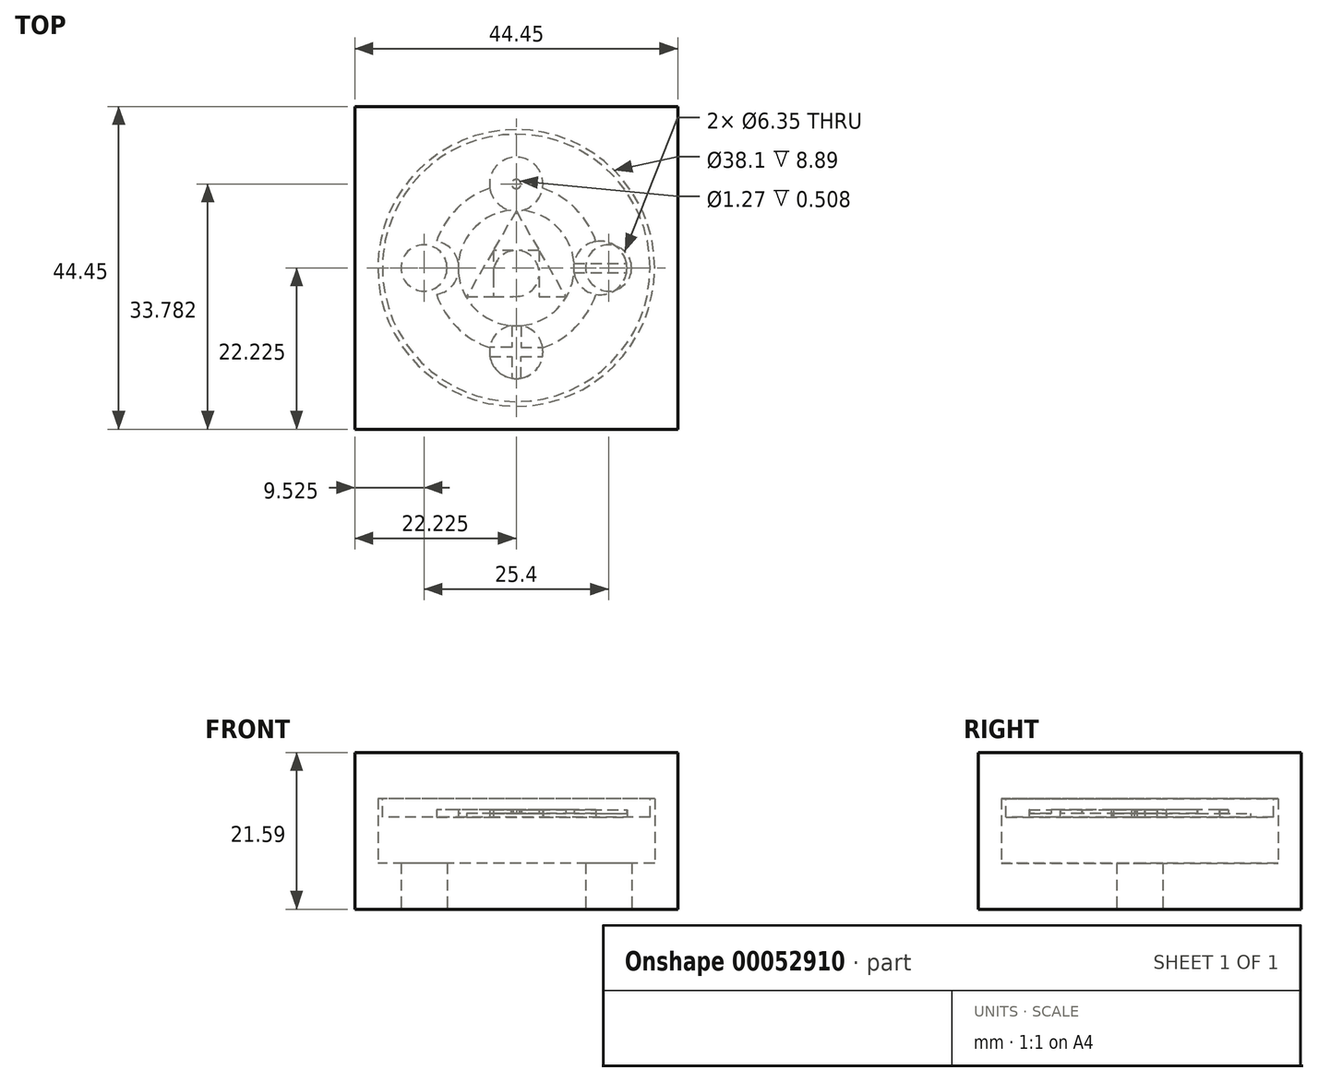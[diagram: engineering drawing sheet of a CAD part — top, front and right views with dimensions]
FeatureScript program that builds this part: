
annotation { "Feature Type Name" : "Feature", "Feature Type Description" : "" }
export const myFeature = defineFeature(function(context is Context, id is Id, definition is map)
    precondition{}
    {
        {
            var Q0;
            Q0=qCreatedBy(makeId("Top.planeOp"),FACE);
            var sketch = newSketch(context, id + "F0", { "sketchPlane" : qUnion([Q0])});
            skLineSegment(sketch, "E0.bottom", {"start": v(0, 0) * mm, "end": v(44.45, 0) * mm});
            skLineSegment(sketch, "E0.top", {"start": v(0, 44.45) * mm, "end": v(44.45, 44.45) * mm});
            skLineSegment(sketch, "E0.left", {"start": v(0, 0) * mm, "end": v(0, 44.45) * mm});
            skLineSegment(sketch, "E0.right", {"start": v(44.45, 0) * mm, "end": v(44.45, 44.45) * mm});
            skCircle(sketch, "E1", {"center": v(22.22, 22.23) * mm, "radius": 19.05 * mm});
            skPoint(sketch, "E1.centerSnap0", {"position": v(0, 22.23) * mm});
            skPoint(sketch, "E1.centerSnap1", {"position": v(22.23, 0) * mm});
            skCircle(sketch, "E2", {"center": v(9.52, 22.23) * mm, "radius": 3.18 * mm});
            skCircle(sketch, "E3", {"center": v(34.92, 22.23) * mm, "radius": 3.18 * mm});
            skSolve(sketch);
        }
        {
            var Q0;
            Q0=makeQuery(id+"F0.imprint","IMPRINT",FACE,{"disambiguationData":[TD([[makeQuery(id+"F0.imprint","IMPRINT",EDGE,{"derivedFrom":sQuery(id+"F0.wireOp",EDGE,"E0.bottom")}),1.0]])]});
            extrude(context, id + "F1", {"entities" : qUnion([Q0]), "depth" : 15.24 * mm});
        }
        {
            var Q0;
            Q0=makeQuery(id+"F0.imprint","IMPRINT",FACE,{"disambiguationData":[TD([[makeQuery(id+"F0.imprint","IMPRINT",EDGE,{"derivedFrom":sQuery(id+"F0.wireOp",EDGE,"E1")}),1.0]])]});
            extrude(context, id + "F2", {"entities" : qUnion([Q0]), "operationType" : NewBodyOperationType.ADD, "depth" : 6.35 * mm});
        }
        {
            var Q0;
            Q0=makeQuery(id+"F1.opExtrude","CAP_FACE",FACE,{"disambiguationData":[OSD([sQuery(id+"F0.wireOp",EDGE,"E0.bottom"),sQuery(id+"F0.wireOp",EDGE,"E0.top"),sQuery(id+"F0.wireOp",EDGE,"E0.left"),sQuery(id+"F0.wireOp",EDGE,"E0.right"),sQuery(id+"F0.wireOp",EDGE,"E1")])],"isStart":false});
            var sketch = newSketch(context, id + "F3", { "sketchPlane" : qUnion([Q0])});
            skCircle(sketch, "E4", {"center": v(22.22, 22.23) * mm, "radius": 18.41 * mm});
            skLineSegment(sketch, "E5.rect.bottom", {"start": v(0, 0) * mm, "end": v(44.45, 0) * mm});
            skLineSegment(sketch, "E5.rect.top", {"start": v(0, 44.45) * mm, "end": v(44.45, 44.45) * mm});
            skLineSegment(sketch, "E5.rect.left", {"start": v(0, 0) * mm, "end": v(0, 44.45) * mm});
            skLineSegment(sketch, "E5.rect.right", {"start": v(44.45, 0) * mm, "end": v(44.45, 44.45) * mm});
            skSolve(sketch);
        }
        {
            var Q0;
            Q0=makeQuery(id+"F3.imprint","IMPRINT",FACE,{"disambiguationData":[TD([[makeQuery(id+"F3.imprint","IMPRINT",EDGE,{"derivedFrom":sQuery(id+"F3.wireOp",EDGE,"E4")}),1.0]])]});
            extrude(context, id + "F4", {"entities" : qUnion([Q0]), "oppositeDirection" : true, "depth" : 2.54 * mm});
        }
        {
            var Q0;
            Q0=makeQuery(id+"F3.imprint","IMPRINT",FACE,{"disambiguationData":[TD([[makeQuery(id+"F3.imprint","IMPRINT",EDGE,{"derivedFrom":sQuery(id+"F3.wireOp",EDGE,"E4")}),1.0]])]});
            var Q1;
            Q1=makeQuery(id+"F3.imprint","IMPRINT",FACE,{"disambiguationData":[TD([[makeQuery(id+"F3.imprint","IMPRINT",EDGE,{"derivedFrom":sQuery(id+"F3.wireOp",EDGE,"E5.rect.bottom")}),1.0]])]});
            var Q2;
            Q2=makeQuery(id+"F3.imprint","IMPRINT",FACE,{"disambiguationData":[TD([[makeQuery(id+"F3.imprint","IMPRINT",EDGE,{"derivedFrom":sQuery(id+"F3.wireOp",EDGE,"E4")}),-1.0]])]});
            extrude(context, id + "F5", {"entities" : qUnion([Q0, Q1, Q2]), "operationType" : NewBodyOperationType.ADD, "depth" : 6.35 * mm});
        }
        {
            var Q0;
            Q0=makeQuery(id+"F4.opExtrude","CAP_FACE",FACE,{"disambiguationData":[OSD([sQuery(id+"F3.wireOp",EDGE,"E4")])],"isStart":false});
            var sketch = newSketch(context, id + "F6", { "sketchPlane" : qUnion([Q0])});
            skCircle(sketch, "E6.0.0", {"center": v(22.22, -22.23) * mm, "radius": 18.41 * mm});
            skArc(sketch, "E7", {"start": v(30.18, -22.86) * mm, "mid": v(30.2, -22.23) * mm, "end": v(30.18, -21.6) * mm});
            skLineSegment(sketch, "E8", {"start": v(15.42, -18.3) * mm, "end": v(21.82, -18.3) * mm});
            skPoint(sketch, "E9.endSnap0", {"position": v(22.22, -18.3) * mm});
            skLineSegment(sketch, "E10", {"start": v(22.23, -30.08) * mm, "end": v(15.42, -18.3) * mm});
            skLineSegment(sketch, "E11.bottom", {"start": v(25.4, -24.64) * mm, "end": v(22.63, -24.64) * mm});
            skLineSegment(sketch, "E11.top", {"start": v(25.4, -18.3) * mm, "end": v(22.63, -18.3) * mm});
            skLineSegment(sketch, "E11.left", {"start": v(25.4, -24.64) * mm, "end": v(25.4, -21.87) * mm});
            skLineSegment(sketch, "E11.right", {"start": v(19.06, -24.64) * mm, "end": v(19.06, -21.87) * mm});
            skCircle(sketch, "E12", {"center": v(22.22, -21.47) * mm, "radius": 3.17 * mm});
            skPoint(sketch, "E12.first.point", {"position": v(25.4, -21.47) * mm});
            skPoint(sketch, "E12.second.point", {"position": v(19.06, -21.47) * mm});
            skPoint(sketch, "E12.third.point", {"position": v(22.22, -24.64) * mm});
            skLineSegment(sketch, "E13", {"start": v(22.22, -30.08) * mm, "end": v(29.03, -18.3) * mm});
            skArc(sketch, "E14", {"start": v(14.28, -21.5) * mm, "mid": v(6.98, -22.23) * mm, "end": v(14.28, -22.95) * mm});
            skArc(sketch, "E15", {"start": v(22.86, -14.3) * mm, "mid": v(22.22, -6.99) * mm, "end": v(21.59, -14.3) * mm});
            skArc(sketch, "E16", {"start": v(30.15, -22.86) * mm, "mid": v(37.46, -22.23) * mm, "end": v(30.15, -21.6) * mm});
            skArc(sketch, "E17", {"start": v(11.25, -25.86) * mm, "mid": v(14.05, -30.4) * mm, "end": v(18.59, -33.2) * mm});
            skArc(sketch, "E18.trimOffspring", {"start": v(18.59, -11.25) * mm, "mid": v(14.05, -14.05) * mm, "end": v(11.25, -18.59) * mm});
            skArc(sketch, "E19.trimOffspring", {"start": v(33.2, -18.59) * mm, "mid": v(30.4, -14.05) * mm, "end": v(25.86, -11.25) * mm});
            skArc(sketch, "E20.trimOffspring", {"start": v(25.86, -33.2) * mm, "mid": v(30.4, -30.4) * mm, "end": v(33.2, -25.86) * mm});
            skCircle(sketch, "E21", {"center": v(22.22, -33.78) * mm, "radius": 0.64 * mm});
            skLineSegment(sketch, "E22", {"start": v(30.15, -22.86) * mm, "end": v(37.4, -22.86) * mm});
            skLineSegment(sketch, "E23", {"start": v(30.15, -21.6) * mm, "end": v(37.4, -21.6) * mm});
            skLineSegment(sketch, "E24", {"start": v(21.59, -14.3) * mm, "end": v(21.59, -11.3) * mm});
            skLineSegment(sketch, "E25", {"start": v(21.59, -11.3) * mm, "end": v(18.6, -11.3) * mm});
            skLineSegment(sketch, "E26", {"start": v(18.6, -10.03) * mm, "end": v(21.59, -10.03) * mm});
            skLineSegment(sketch, "E27", {"start": v(21.59, -10.03) * mm, "end": v(21.59, -7.04) * mm});
            skLineSegment(sketch, "E28", {"start": v(22.86, -7.04) * mm, "end": v(22.86, -10.03) * mm});
            skLineSegment(sketch, "E29", {"start": v(22.86, -10.03) * mm, "end": v(25.85, -10.03) * mm});
            skLineSegment(sketch, "E30", {"start": v(22.86, -14.3) * mm, "end": v(22.86, -11.3) * mm});
            skLineSegment(sketch, "E31", {"start": v(22.86, -11.3) * mm, "end": v(25.85, -11.3) * mm});
            skArc(sketch, "E32.trimOffspring", {"start": v(21.5, -30.17) * mm, "mid": v(22.22, -37.46) * mm, "end": v(22.95, -30.17) * mm});
            skArc(sketch, "E33.trimOffspring", {"start": v(30.17, -21.5) * mm, "mid": v(27.87, -16.58) * mm, "end": v(22.95, -14.28) * mm});
            skArc(sketch, "E34.trimOffspring", {"start": v(22.86, -14.27) * mm, "mid": v(22.23, -14.25) * mm, "end": v(21.59, -14.27) * mm});
            skArc(sketch, "E35.trimOffspring", {"start": v(21.5, -14.28) * mm, "mid": v(16.58, -27.87) * mm, "end": v(30.17, -22.95) * mm});
            skLineSegment(sketch, "E36", {"start": v(19.06, -21.87) * mm, "end": v(19.08, -21.87) * mm});
            skLineSegment(sketch, "E37", {"start": v(19.06, -21.07) * mm, "end": v(19.08, -21.07) * mm});
            skLineSegment(sketch, "E38", {"start": v(21.82, -18.32) * mm, "end": v(21.82, -18.3) * mm});
            skLineSegment(sketch, "E39", {"start": v(22.63, -18.32) * mm, "end": v(22.63, -18.3) * mm});
            skLineSegment(sketch, "E40", {"start": v(25.37, -21.07) * mm, "end": v(25.4, -21.07) * mm});
            skLineSegment(sketch, "E41", {"start": v(25.37, -21.87) * mm, "end": v(25.4, -21.87) * mm});
            skLineSegment(sketch, "E42", {"start": v(22.63, -24.61) * mm, "end": v(22.63, -24.64) * mm});
            skLineSegment(sketch, "E43", {"start": v(21.82, -24.61) * mm, "end": v(21.82, -24.64) * mm});
            skLineSegment(sketch, "E44.trimOffspring", {"start": v(19.06, -21.07) * mm, "end": v(19.06, -18.3) * mm});
            skLineSegment(sketch, "E45.trimOffspring", {"start": v(21.82, -24.64) * mm, "end": v(19.06, -24.64) * mm});
            skLineSegment(sketch, "E46.trimOffspring", {"start": v(25.4, -21.07) * mm, "end": v(25.4, -18.3) * mm});
            skLineSegment(sketch, "E47.trimOffspring", {"start": v(21.82, -18.3) * mm, "end": v(19.06, -18.3) * mm});
            skLineSegment(sketch, "E48.trimOffspring", {"start": v(22.63, -18.3) * mm, "end": v(29.03, -18.3) * mm});
            skSolve(sketch);
        }
        {
            var Q0;
            {var subQ0=sQuery(id+"F6.wireOp",EDGE,"E26");Q0=makeQuery(id+"F6.imprint","IMPRINT",FACE,{"disambiguationData":[TD([[makeQuery(id+"F6.imprint","IMPRINT",EDGE,{"derivedFrom":subQ0}),1.0]])]});}
            var Q1;
            {var subQ0=sQuery(id+"F6.wireOp",EDGE,"E28");Q1=makeQuery(id+"F6.imprint","IMPRINT",FACE,{"disambiguationData":[TD([[makeQuery(id+"F6.imprint","IMPRINT",EDGE,{"derivedFrom":subQ0}),1.0]])]});}
            var Q2;
            Q2=makeQuery(id+"F6.imprint","IMPRINT",FACE,{"disambiguationData":[TD([[makeQuery(id+"F6.imprint","IMPRINT",EDGE,{"derivedFrom":sQuery(id+"F6.wireOp",EDGE,"E21")}),-1.0]])]});
            var Q3;
            {var subQ4=sQuery(id+"F6.wireOp",EDGE,"E31");Q3=makeQuery(id+"F6.imprint","IMPRINT",FACE,{"disambiguationData":[TD([[makeQuery(id+"F6.imprint","IMPRINT",EDGE,{"derivedFrom":subQ4}),-1.0]])]});}
            var Q4;
            {var subQ0=sQuery(id+"F6.wireOp",EDGE,"E25");Q4=makeQuery(id+"F6.imprint","IMPRINT",FACE,{"disambiguationData":[TD([[makeQuery(id+"F6.imprint","IMPRINT",EDGE,{"derivedFrom":subQ0}),1.0]])]});}
            var Q5;
            {var subQ1=sQuery(id+"F6.wireOp",EDGE,"E16");var subQ4=makeQuery(id+"F6.imprint","INTERSECT",VERTEX,{"derivedFrom":[subQ1,sQuery(id+"F6.wireOp",EDGE,"E19.trimOffspring")]});Q5=makeQuery(id+"F6.imprint","IMPRINT",FACE,{"disambiguationData":[TD([[makeQuery(id+"F6.imprint","IMPRINT",EDGE,{"disambiguationData":[TD([[subQ4,1.0]])],"derivedFrom":subQ1}),1.0]])]});}
            var Q6;
            {var subQ0=sQuery(id+"F6.wireOp",EDGE,"E22");var subQ2=sQuery(id+"F6.wireOp",EDGE,"E16");var subQ3=makeQuery(id+"F6.imprint","INTERSECT",VERTEX,{"disambiguationData":[OD(0.0)],"derivedFrom":[subQ2,subQ0]});Q6=makeQuery(id+"F6.imprint","IMPRINT",FACE,{"disambiguationData":[TD([[makeQuery(id+"F6.imprint","IMPRINT",EDGE,{"disambiguationData":[TD([[subQ3,-1.0]])],"derivedFrom":subQ2}),1.0]])]});}
            var Q7;
            {var subQ0=sQuery(id+"F6.wireOp",EDGE,"E35.trimOffspring");var subQ1=sQuery(id+"F6.wireOp",EDGE,"E14");var subQ2=makeQuery(id+"F6.imprint","INTERSECT",VERTEX,{"disambiguationData":[OD(0.0)],"derivedFrom":[subQ1,subQ0]});Q7=makeQuery(id+"F6.imprint","IMPRINT",FACE,{"disambiguationData":[TD([[makeQuery(id+"F6.imprint","IMPRINT",EDGE,{"disambiguationData":[TD([[subQ2,-1.0]])],"derivedFrom":subQ1}),1.0]])]});}
            var Q8;
            {var subQ5=sQuery(id+"F6.wireOp",EDGE,"E37");Q8=makeQuery(id+"F6.imprint","IMPRINT",FACE,{"disambiguationData":[TD([[makeQuery(id+"F6.imprint","IMPRINT",EDGE,{"derivedFrom":subQ5}),1.0]])]});}
            var Q9;
            {var subQ5=sQuery(id+"F6.wireOp",EDGE,"E36");Q9=makeQuery(id+"F6.imprint","IMPRINT",FACE,{"disambiguationData":[TD([[makeQuery(id+"F6.imprint","IMPRINT",EDGE,{"derivedFrom":subQ5}),-1.0]])]});}
            var Q10;
            {var subQ1=sQuery(id+"F6.wireOp",EDGE,"E11.bottom");var subQ3=sQuery(id+"F6.wireOp",EDGE,"E12");var subQ4=makeQuery(id+"F6.imprint","INTERSECT",VERTEX,{"derivedFrom":[subQ1,subQ3]});Q10=makeQuery(id+"F6.imprint","IMPRINT",FACE,{"disambiguationData":[TD([[makeQuery(id+"F6.imprint","IMPRINT",EDGE,{"disambiguationData":[TD([[subQ4,-1.0]])],"derivedFrom":subQ3}),-1.0]])]});}
            var Q11;
            {var subQ1=sQuery(id+"F6.wireOp",EDGE,"E11.top");var subQ3=sQuery(id+"F6.wireOp",EDGE,"E12");var subQ4=makeQuery(id+"F6.imprint","INTERSECT",VERTEX,{"derivedFrom":[subQ1,subQ3]});Q11=makeQuery(id+"F6.imprint","IMPRINT",FACE,{"disambiguationData":[TD([[makeQuery(id+"F6.imprint","IMPRINT",EDGE,{"disambiguationData":[TD([[subQ4,1.0]])],"derivedFrom":subQ3}),-1.0]])]});}
            var Q12;
            {var subQ5=sQuery(id+"F6.wireOp",EDGE,"E41");Q12=makeQuery(id+"F6.imprint","IMPRINT",FACE,{"disambiguationData":[TD([[makeQuery(id+"F6.imprint","IMPRINT",EDGE,{"derivedFrom":subQ5}),-1.0]])]});}
            var Q13;
            {var subQ10=sQuery(id+"F6.wireOp",EDGE,"E7");Q13=makeQuery(id+"F6.imprint","IMPRINT",FACE,{"disambiguationData":[TD([[makeQuery(id+"F6.imprint","IMPRINT",EDGE,{"derivedFrom":subQ10}),1.0]])]});}
            var Q14;
            {var subQ0=sQuery(id+"F6.wireOp",EDGE,"E11.left");var subQ1=sQuery(id+"F6.wireOp",EDGE,"E11.bottom");var subQ2=makeQuery(id+"F6.imprint","INTERSECT",VERTEX,{"derivedFrom":[subQ1,subQ0]});Q14=makeQuery(id+"F6.imprint","IMPRINT",FACE,{"disambiguationData":[TD([[makeQuery(id+"F6.imprint","IMPRINT",EDGE,{"disambiguationData":[TD([[subQ2,-1.0]])],"derivedFrom":subQ1}),-1.0]])]});}
            var Q15;
            {var subQ0=sQuery(id+"F6.wireOp",EDGE,"E45.trimOffspring");var subQ1=sQuery(id+"F6.wireOp",EDGE,"E10");var subQ2=makeQuery(id+"F6.imprint","INTERSECT",VERTEX,{"derivedFrom":[subQ1,subQ0]});Q15=makeQuery(id+"F6.imprint","IMPRINT",FACE,{"disambiguationData":[TD([[makeQuery(id+"F6.imprint","IMPRINT",EDGE,{"disambiguationData":[TD([[subQ2,-1.0]])],"derivedFrom":subQ1}),1.0]])]});}
            extrude(context, id + "F7", {"entities" : qUnion([Q0, Q1, Q2, Q3, Q4, Q5, Q6, Q7, Q8, Q9, Q10, Q11, Q12, Q13, Q14, Q15]), "operationType" : NewBodyOperationType.REMOVE, "oppositeDirection" : true, "depth" : 0.5 * mm});
        }
        {
            var Q0;
            {var subQ0=sQuery(id+"F6.wireOp",EDGE,"E18.trimOffspring");Q0=makeQuery(id+"F6.imprint","IMPRINT",FACE,{"disambiguationData":[TD([[makeQuery(id+"F6.imprint","IMPRINT",EDGE,{"derivedFrom":subQ0}),1.0]])]});}
            var Q1;
            {var subQ3=sQuery(id+"F6.wireOp",EDGE,"E17");Q1=makeQuery(id+"F6.imprint","IMPRINT",FACE,{"disambiguationData":[TD([[makeQuery(id+"F6.imprint","IMPRINT",EDGE,{"derivedFrom":subQ3}),1.0]])]});}
            var Q2;
            {var subQ0=sQuery(id+"F6.wireOp",EDGE,"E19.trimOffspring");Q2=makeQuery(id+"F6.imprint","IMPRINT",FACE,{"disambiguationData":[TD([[makeQuery(id+"F6.imprint","IMPRINT",EDGE,{"derivedFrom":subQ0}),1.0]])]});}
            var Q3;
            {var subQ5=sQuery(id+"F6.wireOp",EDGE,"E25");Q3=makeQuery(id+"F6.imprint","IMPRINT",FACE,{"disambiguationData":[TD([[makeQuery(id+"F6.imprint","IMPRINT",EDGE,{"derivedFrom":subQ5}),-1.0]])]});}
            var Q4;
            {var subQ0=sQuery(id+"F6.wireOp",EDGE,"E7");Q4=makeQuery(id+"F6.imprint","IMPRINT",FACE,{"disambiguationData":[TD([[makeQuery(id+"F6.imprint","IMPRINT",EDGE,{"derivedFrom":subQ0}),-1.0]])]});}
            var Q5;
            Q5=makeQuery(id+"F6.imprint","IMPRINT",FACE,{"disambiguationData":[TD([[makeQuery(id+"F6.imprint","IMPRINT",EDGE,{"derivedFrom":sQuery(id+"F6.wireOp",EDGE,"E21")}),1.0]])]});
            var Q6;
            {var subQ0=sQuery(id+"F6.wireOp",EDGE,"E12");var subQ6=makeQuery(id+"F6.imprint","INTERSECT",VERTEX,{"derivedFrom":[subQ0,sQuery(id+"F6.wireOp",EDGE,"E39")]});Q6=makeQuery(id+"F6.imprint","IMPRINT",FACE,{"disambiguationData":[TD([[makeQuery(id+"F6.imprint","IMPRINT",EDGE,{"disambiguationData":[TD([[subQ6,1.0]])],"derivedFrom":subQ0}),1.0]])]});}
            var Q7;
            {var subQ5=sQuery(id+"F6.wireOp",EDGE,"E42");Q7=makeQuery(id+"F6.imprint","IMPRINT",FACE,{"disambiguationData":[TD([[makeQuery(id+"F6.imprint","IMPRINT",EDGE,{"derivedFrom":subQ5}),-1.0]])]});}
            var Q8;
            {var subQ0=sQuery(id+"F6.wireOp",EDGE,"E40");Q8=makeQuery(id+"F6.imprint","IMPRINT",FACE,{"disambiguationData":[TD([[makeQuery(id+"F6.imprint","IMPRINT",EDGE,{"derivedFrom":subQ0}),-1.0]])]});}
            var Q9;
            {var subQ4=sQuery(id+"F6.wireOp",EDGE,"E8");Q9=makeQuery(id+"F6.imprint","IMPRINT",FACE,{"disambiguationData":[TD([[makeQuery(id+"F6.imprint","IMPRINT",EDGE,{"derivedFrom":subQ4}),-1.0]])]});}
            var Q10;
            {var subQ0=sQuery(id+"F6.wireOp",EDGE,"E20.trimOffspring");Q10=makeQuery(id+"F6.imprint","IMPRINT",FACE,{"disambiguationData":[TD([[makeQuery(id+"F6.imprint","IMPRINT",EDGE,{"derivedFrom":subQ0}),1.0]])]});}
            extrude(context, id + "F8", {"entities" : qUnion([Q0, Q1, Q2, Q3, Q4, Q5, Q6, Q7, Q8, Q9, Q10]), "operationType" : NewBodyOperationType.REMOVE, "oppositeDirection" : true, "depth" : 1.02 * mm});
        }
    });
